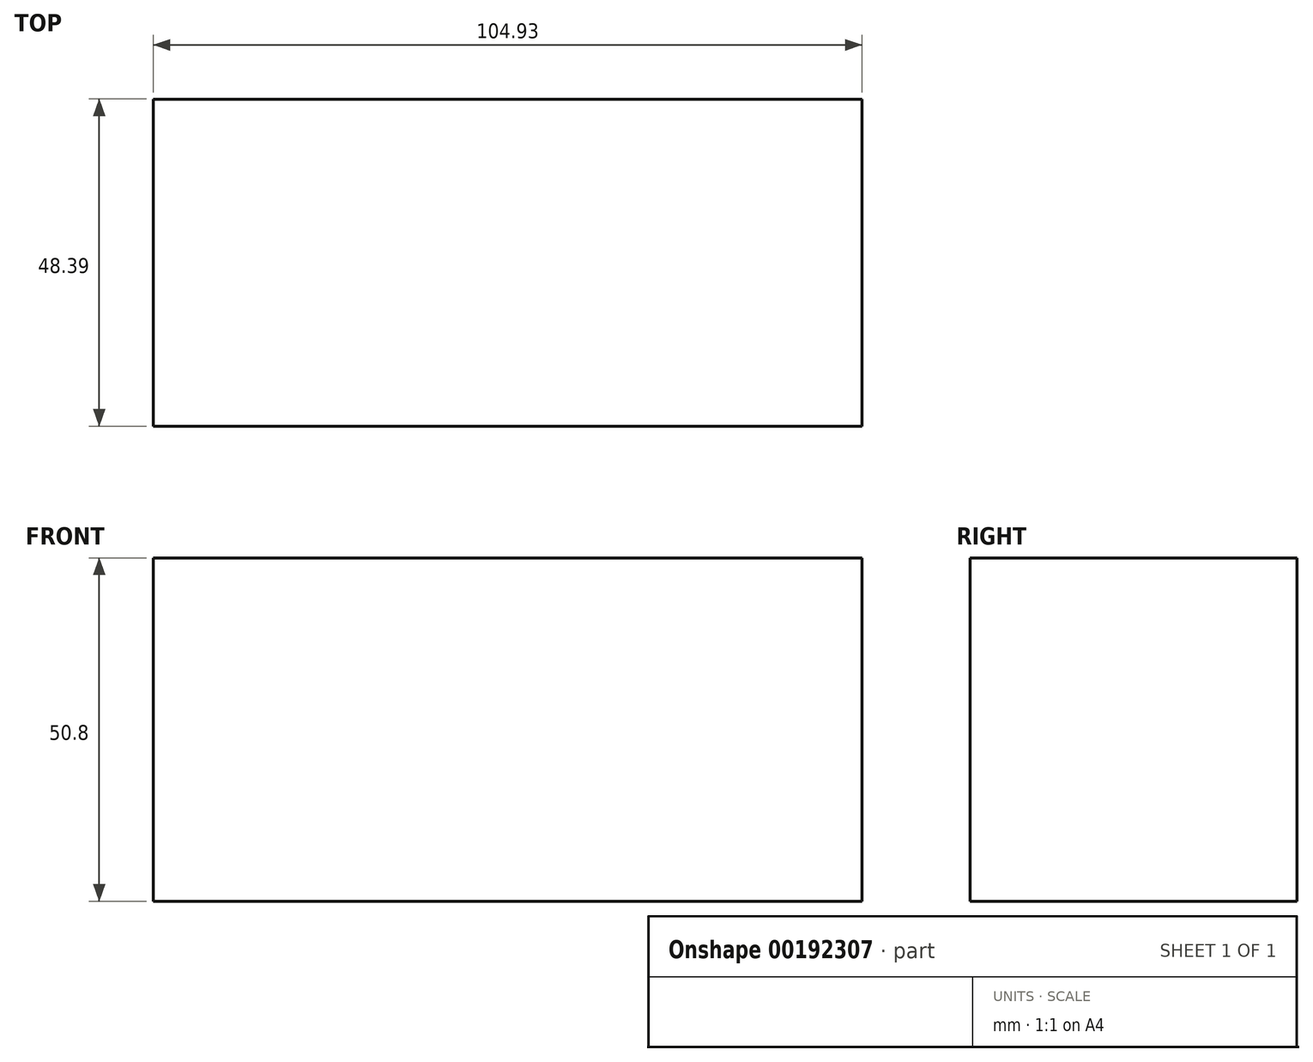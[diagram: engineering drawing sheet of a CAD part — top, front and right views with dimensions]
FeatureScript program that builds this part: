
annotation { "Feature Type Name" : "Feature", "Feature Type Description" : "" }
export const myFeature = defineFeature(function(context is Context, id is Id, definition is map)
    precondition{}
    {
        {
            var Q0;
            Q0=qCreatedBy(makeId("Top.planeOp"),FACE);
            var sketch = newSketch(context, id + "F0", { "sketchPlane" : qUnion([Q0])});
            skLineSegment(sketch, "E0.bottom", {"start": v(-44.8, 22.52) * mm, "end": v(60.13, 22.52) * mm});
            skLineSegment(sketch, "E0.top", {"start": v(-44.8, -25.87) * mm, "end": v(60.13, -25.87) * mm});
            skLineSegment(sketch, "E0.left", {"start": v(-44.8, 22.52) * mm, "end": v(-44.8, -25.87) * mm});
            skLineSegment(sketch, "E0.right", {"start": v(60.13, 22.52) * mm, "end": v(60.13, -25.87) * mm});
            skSolve(sketch);
        }
        {
            var Q0;
            Q0=makeQuery(id+"F0.imprint","IMPRINT",FACE,{"disambiguationData":[TD([[makeQuery(id+"F0.imprint","IMPRINT",EDGE,{"derivedFrom":sQuery(id+"F0.wireOp",EDGE,"E0.bottom")}),-1.0]])]});
            extrude(context, id + "F1", {"entities" : qUnion([Q0]), "depth" : 25.4 * mm, "hasSecondDirection" : true, "secondDirectionOppositeDirection" : true, "secondDirectionDepth" : 25.4 * mm});
        }
    });
